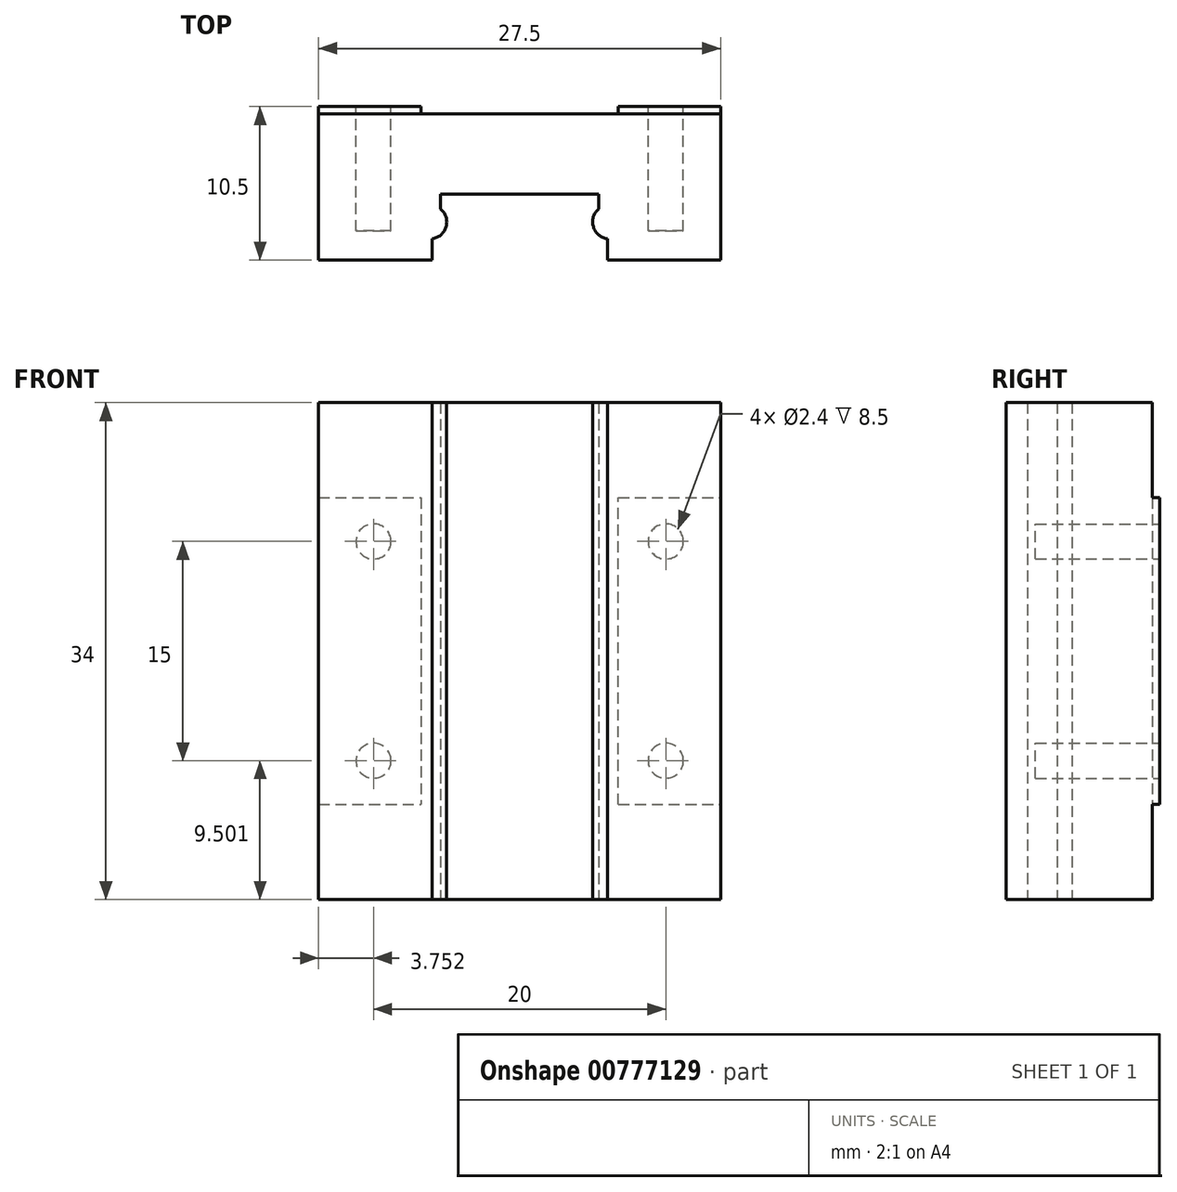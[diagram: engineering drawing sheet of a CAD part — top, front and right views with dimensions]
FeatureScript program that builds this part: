
annotation { "Feature Type Name" : "Feature", "Feature Type Description" : "" }
export const myFeature = defineFeature(function(context is Context, id is Id, definition is map)
    precondition{}
    {
        {
            var Q0;
            Q0=qCreatedBy(makeId("Front.planeOp"),FACE);
            var sketch = newSketch(context, id + "F0", { "sketchPlane" : qUnion([Q0])});
            skLineSegment(sketch, "E0.bottom", {"start": v(-53.4, 37.41) * mm, "end": v(-25.9, 37.41) * mm});
            skLineSegment(sketch, "E0.top", {"start": v(-53.4, 3.41) * mm, "end": v(-25.9, 3.41) * mm});
            skLineSegment(sketch, "E0.left", {"start": v(-53.4, 37.41) * mm, "end": v(-53.4, 3.41) * mm});
            skLineSegment(sketch, "E0.right", {"start": v(-25.9, 37.41) * mm, "end": v(-25.9, 3.41) * mm});
            skCircle(sketch, "E1", {"center": v(-49.66, 27.91) * mm, "radius": 1.2 * mm});
            skCircle(sketch, "E2", {"center": v(-49.66, 12.91) * mm, "radius": 1.2 * mm});
            skCircle(sketch, "E3", {"center": v(-29.66, 12.91) * mm, "radius": 1.2 * mm});
            skCircle(sketch, "E4", {"center": v(-29.66, 27.91) * mm, "radius": 1.2 * mm});
            skLineSegment(sketch, "E5.top", {"start": v(-53.4, 30.91) * mm, "end": v(-25.9, 30.91) * mm});
            skLineSegment(sketch, "E5.left", {"start": v(-53.4, 37.41) * mm, "end": v(-53.4, 30.91) * mm});
            skLineSegment(sketch, "E5.right", {"start": v(-25.9, 37.41) * mm, "end": v(-25.9, 30.91) * mm});
            skLineSegment(sketch, "E6.top", {"start": v(-53.4, 9.91) * mm, "end": v(-25.9, 9.91) * mm});
            skLineSegment(sketch, "E6.left", {"start": v(-53.4, 3.41) * mm, "end": v(-53.4, 9.91) * mm});
            skLineSegment(sketch, "E6.right", {"start": v(-25.9, 3.41) * mm, "end": v(-25.9, 9.91) * mm});
            skLineSegment(sketch, "E7.bottom", {"start": v(-53.4, 37.41) * mm, "end": v(-46.4, 37.41) * mm});
            skLineSegment(sketch, "E7.top", {"start": v(-53.4, 3.41) * mm, "end": v(-46.4, 3.41) * mm});
            skLineSegment(sketch, "E7.right", {"start": v(-46.4, 37.41) * mm, "end": v(-46.4, 3.41) * mm});
            skLineSegment(sketch, "E8.bottom", {"start": v(-32.9, 3.41) * mm, "end": v(-25.9, 3.41) * mm});
            skLineSegment(sketch, "E8.top", {"start": v(-32.9, 37.41) * mm, "end": v(-25.9, 37.41) * mm});
            skLineSegment(sketch, "E8.left", {"start": v(-32.9, 3.41) * mm, "end": v(-32.9, 37.41) * mm});
            skLineSegment(sketch, "E8.right", {"start": v(-25.9, 3.41) * mm, "end": v(-25.9, 37.41) * mm});
            skSolve(sketch);
        }
        {
            var Q0;
            Q0 = qSketchRegion(id + "F0", true);
            var Q1;
            {var subQ0=sQuery(id+"F0.wireOp",EDGE,"E7.right");var subQ1=sQuery(id+"F0.wireOp",EDGE,"E5.top");var subQ2=makeQuery(id+"F0.imprint","INTERSECT",VERTEX,{"derivedFrom":[subQ1,subQ0]});Q1=makeQuery(id+"F0.imprint","IMPRINT",FACE,{"disambiguationData":[TD([[makeQuery(id+"F0.imprint","IMPRINT",EDGE,{"disambiguationData":[TD([[subQ2,-1.0]])],"derivedFrom":subQ1}),-1.0]])]});}
            var Q2;
            Q2=makeQuery(id+"F0.imprint","IMPRINT",FACE,{"disambiguationData":[TD([[makeQuery(id+"F0.imprint","IMPRINT",EDGE,{"derivedFrom":sQuery(id+"F0.wireOp",EDGE,"E1")}),1.0]])]});
            var Q3;
            Q3=makeQuery(id+"F0.imprint","IMPRINT",FACE,{"disambiguationData":[TD([[makeQuery(id+"F0.imprint","IMPRINT",EDGE,{"derivedFrom":sQuery(id+"F0.wireOp",EDGE,"E2")}),1.0]])]});
            var Q4;
            Q4=makeQuery(id+"F0.imprint","IMPRINT",FACE,{"disambiguationData":[TD([[makeQuery(id+"F0.imprint","IMPRINT",EDGE,{"derivedFrom":sQuery(id+"F0.wireOp",EDGE,"E3")}),1.0]])]});
            var Q5;
            Q5=makeQuery(id+"F0.imprint","IMPRINT",FACE,{"disambiguationData":[TD([[makeQuery(id+"F0.imprint","IMPRINT",EDGE,{"derivedFrom":sQuery(id+"F0.wireOp",EDGE,"E4")}),1.0]])]});
            extrude(context, id + "F1", {"entities" : qUnion([Q0, Q1, Q2, Q3, Q4, Q5]), "depth" : 10 * mm, "offsetDistance" : 25 * mm});
        }
        {
            var Q0;
            Q0 = qSketchRegion(id + "F0", true);
            var Q1;
            Q1=makeQuery(id+"F1.opExtrude","CAP_FACE",FACE,{"disambiguationData":[OSD([sQuery(id+"F0.wireOp",EDGE,"E0.bottom"),sQuery(id+"F0.wireOp",EDGE,"E0.top"),sQuery(id+"F0.wireOp",EDGE,"E7.bottom"),sQuery(id+"F0.wireOp",EDGE,"E7.top"),sQuery(id+"F0.wireOp",EDGE,"E0.left"),sQuery(id+"F0.wireOp",EDGE,"E8.bottom"),sQuery(id+"F0.wireOp",EDGE,"E8.top"),sQuery(id+"F0.wireOp",EDGE,"E8.right")])],"isStart":false});
            var Q2;
            Q2=makeQuery(id+"F0.imprint","IMPRINT",FACE,{"disambiguationData":[TD([[makeQuery(id+"F0.imprint","IMPRINT",EDGE,{"derivedFrom":sQuery(id+"F0.wireOp",EDGE,"E4")}),1.0]])]});
            var Q3;
            Q3=makeQuery(id+"F0.imprint","IMPRINT",FACE,{"disambiguationData":[TD([[makeQuery(id+"F0.imprint","IMPRINT",EDGE,{"derivedFrom":sQuery(id+"F0.wireOp",EDGE,"E1")}),1.0]])]});
            var Q4;
            Q4=makeQuery(id+"F0.imprint","IMPRINT",FACE,{"disambiguationData":[TD([[makeQuery(id+"F0.imprint","IMPRINT",EDGE,{"derivedFrom":sQuery(id+"F0.wireOp",EDGE,"E2")}),1.0]])]});
            var Q5;
            Q5=makeQuery(id+"F0.imprint","IMPRINT",FACE,{"disambiguationData":[TD([[makeQuery(id+"F0.imprint","IMPRINT",EDGE,{"derivedFrom":sQuery(id+"F0.wireOp",EDGE,"E3")}),1.0]])]});
            extrude(context, id + "F2", {"entities" : qUnion([Q0, Q1, Q2, Q3, Q4, Q5]), "operationType" : NewBodyOperationType.ADD, "oppositeDirection" : true, "depth" : .5 * mm, "offsetDistance" : 25 * mm});
        }
        {
            var Q0;
            {var subQ5=sQuery(id+"F0.wireOp",EDGE,"E8.top");Q0=makeQuery(id+"F0.imprint","IMPRINT",FACE,{"disambiguationData":[TD([[makeQuery(id+"F0.imprint","IMPRINT",EDGE,{"derivedFrom":subQ5}),-1.0]])]});}
            var Q1;
            {var subQ0=sQuery(id+"F0.wireOp",EDGE,"E0.bottom");Q1=makeQuery(id+"F0.imprint","IMPRINT",FACE,{"disambiguationData":[TD([[makeQuery(id+"F0.imprint","IMPRINT",EDGE,{"derivedFrom":subQ0}),-1.0]])]});}
            var Q2;
            {var subQ5=sQuery(id+"F0.wireOp",EDGE,"E7.bottom");Q2=makeQuery(id+"F0.imprint","IMPRINT",FACE,{"disambiguationData":[TD([[makeQuery(id+"F0.imprint","IMPRINT",EDGE,{"derivedFrom":subQ5}),-1.0]])]});}
            var Q3;
            {var subQ5=sQuery(id+"F0.wireOp",EDGE,"E7.top");Q3=makeQuery(id+"F0.imprint","IMPRINT",FACE,{"disambiguationData":[TD([[makeQuery(id+"F0.imprint","IMPRINT",EDGE,{"derivedFrom":subQ5}),1.0]])]});}
            var Q4;
            {var subQ0=sQuery(id+"F0.wireOp",EDGE,"E0.top");Q4=makeQuery(id+"F0.imprint","IMPRINT",FACE,{"disambiguationData":[TD([[makeQuery(id+"F0.imprint","IMPRINT",EDGE,{"derivedFrom":subQ0}),1.0]])]});}
            var Q5;
            {var subQ5=sQuery(id+"F0.wireOp",EDGE,"E8.bottom");Q5=makeQuery(id+"F0.imprint","IMPRINT",FACE,{"disambiguationData":[TD([[makeQuery(id+"F0.imprint","IMPRINT",EDGE,{"derivedFrom":subQ5}),1.0]])]});}
            extrude(context, id + "F3", {"entities" : qUnion([Q0, Q1, Q2, Q3, Q4, Q5]), "operationType" : NewBodyOperationType.REMOVE, "oppositeDirection" : true, "depth" : 1 * mm, "offsetDistance" : 25 * mm});
        }
        {
            var Q0;
            Q0=makeQuery(id+"F0.imprint","IMPRINT",FACE,{"disambiguationData":[TD([[makeQuery(id+"F0.imprint","IMPRINT",EDGE,{"derivedFrom":sQuery(id+"F0.wireOp",EDGE,"E4")}),1.0]])]});
            var Q1;
            Q1=makeQuery(id+"F0.imprint","IMPRINT",FACE,{"disambiguationData":[TD([[makeQuery(id+"F0.imprint","IMPRINT",EDGE,{"derivedFrom":sQuery(id+"F0.wireOp",EDGE,"E3")}),1.0]])]});
            var Q2;
            Q2=makeQuery(id+"F0.imprint","IMPRINT",FACE,{"disambiguationData":[TD([[makeQuery(id+"F0.imprint","IMPRINT",EDGE,{"derivedFrom":sQuery(id+"F0.wireOp",EDGE,"E2")}),1.0]])]});
            var Q3;
            Q3=makeQuery(id+"F0.imprint","IMPRINT",FACE,{"disambiguationData":[TD([[makeQuery(id+"F0.imprint","IMPRINT",EDGE,{"derivedFrom":sQuery(id+"F0.wireOp",EDGE,"E1")}),1.0]])]});
            extrude(context, id + "F4", {"entities" : qUnion([Q0, Q1, Q2, Q3]), "operationType" : NewBodyOperationType.REMOVE, "depth" : 8 * mm, "offsetDistance" : 25 * mm, "hasSecondDirection" : true, "secondDirectionOppositeDirection" : true, "secondDirectionDepth" : 1 * mm});
        }
        {
            var Q0;
            {var subQ0=sQuery(id+"F0.wireOp",EDGE,"E8.bottom");var subQ1=sQuery(id+"F0.wireOp",EDGE,"E7.top");var subQ2=sQuery(id+"F0.wireOp",EDGE,"E0.top");Q0=makeQuery(id+"F2.boolean.opBoolean","MERGE",FACE,{"derivedFrom":[makeQuery(id+"F1.opExtrude","SWEPT_FACE",FACE,{"disambiguationData":[OSD([subQ2,subQ1,subQ0])]}),makeQuery(id+"F2.opExtrude","SWEPT_FACE",FACE,{"disambiguationData":[OSD([subQ2,subQ1,subQ0]),TDD([makeQuery(id+"F0.imprint","IMPRINT",EDGE,{"derivedFrom":subQ2}),makeQuery(id+"F0.imprint","IMPRINT",EDGE,{"derivedFrom":subQ1}),makeQuery(id+"F0.imprint","IMPRINT",EDGE,{"derivedFrom":subQ0})])]})]});}
            var sketch = newSketch(context, id + "F5", { "sketchPlane" : qUnion([Q0])});
            skLineSegment(sketch, "E9", {"start": v(-33.66, 10) * mm, "end": v(-33.66, 8.55) * mm});
            skLineSegment(sketch, "E10", {"start": v(-34.26, 6.5) * mm, "end": v(-34.26, 5.5) * mm});
            skLineSegment(sketch, "E11", {"start": v(-34.26, 5.5) * mm, "end": v(-45.06, 5.5) * mm});
            skLineSegment(sketch, "E12", {"start": v(-45.06, 5.5) * mm, "end": v(-45.06, 6.5) * mm});
            skLineSegment(sketch, "E13", {"start": v(-45.66, 8.55) * mm, "end": v(-45.66, 10) * mm});
            skArc(sketch, "E14", {"start": v(-33.66, 8.55) * mm, "mid": v(-34.6, 7.71) * mm, "end": v(-34.26, 6.5) * mm});
            skArc(sketch, "E15", {"start": v(-45.06, 6.5) * mm, "mid": v(-44.69, 7.72) * mm, "end": v(-45.66, 8.55) * mm});
            skSolve(sketch);
        }
        {
            var Q0;
            Q0 = qSketchRegion(id + "F5", true);
            var Q1;
            {var subQ0=sQuery(id+"F5.wireOp",EDGE,"E9");Q1=makeQuery(id+"F5.imprint","IMPRINT",FACE,{"disambiguationData":[TD([[makeQuery(id+"F5.imprint","IMPRINT",EDGE,{"derivedFrom":subQ0}),-1.0]])]});}
            extrude(context, id + "F6", {"entities" : qUnion([Q0, Q1]), "operationType" : NewBodyOperationType.REMOVE, "endBound" : BoundingType.THROUGH_ALL, "oppositeDirection" : true, "depth" : 25 * mm, "offsetDistance" : 25 * mm});
        }
    });
